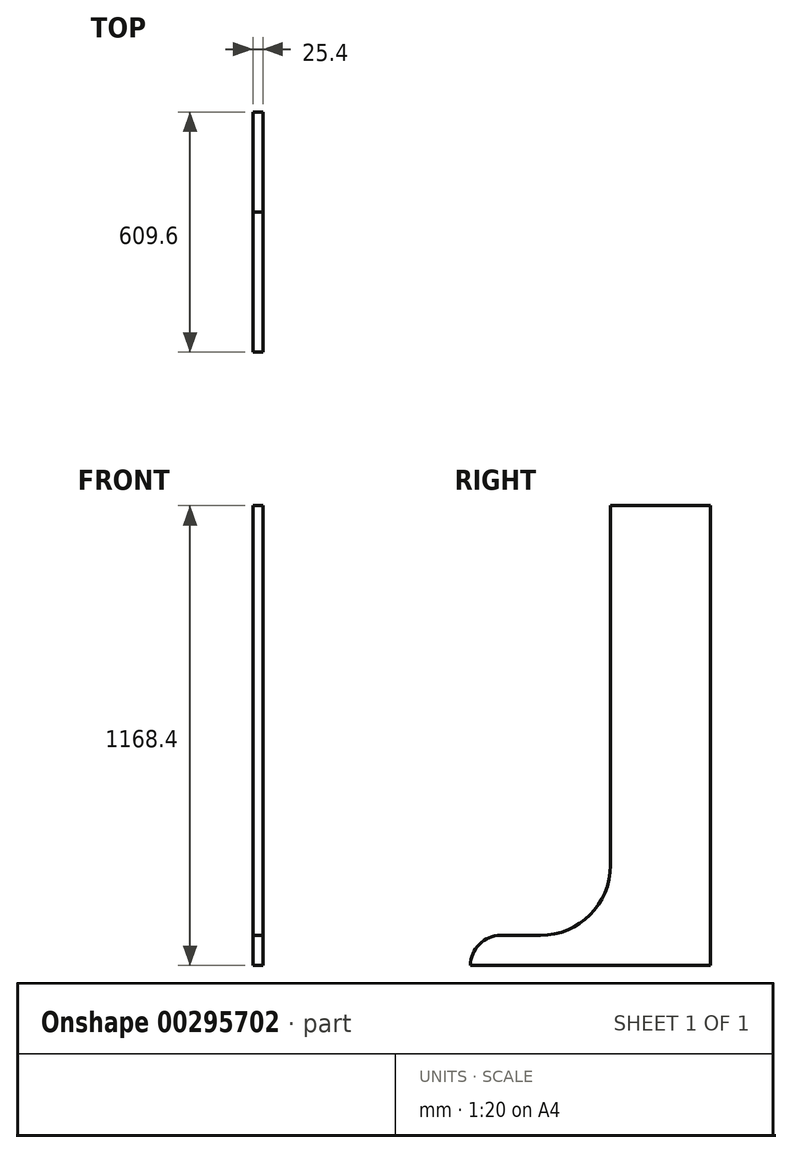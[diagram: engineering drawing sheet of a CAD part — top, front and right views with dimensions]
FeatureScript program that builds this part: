
annotation { "Feature Type Name" : "Feature", "Feature Type Description" : "" }
export const myFeature = defineFeature(function(context is Context, id is Id, definition is map)
    precondition{}
    {
        {
            var Q0;
            Q0=qCreatedBy(makeId("Right.planeOp"),FACE);
            var sketch = newSketch(context, id + "F0", { "sketchPlane" : qUnion([Q0])});
            skLineSegment(sketch, "E0.bottom", {"start": v(127, 584.2) * mm, "end": v(-127, 584.2) * mm});
            skLineSegment(sketch, "E0.top", {"start": v(127, -584.2) * mm, "end": v(-127, -584.2) * mm});
            skLineSegment(sketch, "E0.left", {"start": v(127, 584.2) * mm, "end": v(127, -584.2) * mm});
            skLineSegment(sketch, "E0.right", {"start": v(-127, 584.2) * mm, "end": v(-127, -584.2) * mm});
            skPoint(sketch, "E0.middle", {"position": v(0, 0) * mm});
            skLineSegment(sketch, "E1.bottom", {"start": v(-127, -584.2) * mm, "end": v(-482.6, -584.2) * mm});
            skLineSegment(sketch, "E1.top", {"start": v(-127, -330.2) * mm, "end": v(-482.6, -330.2) * mm});
            skLineSegment(sketch, "E1.left", {"start": v(-127, -584.2) * mm, "end": v(-127, -330.2) * mm});
            skLineSegment(sketch, "E1.right", {"start": v(-482.6, -584.2) * mm, "end": v(-482.6, -330.2) * mm});
            skSolve(sketch);
        }
        {
            var Q0;
            Q0 = qSketchRegion(id + "F0", true);
            extrude(context, id + "F1", {"entities" : qUnion([Q0]), "endBound" : BoundingType.SYMMETRIC, "depth" : 25.4 * mm});
        }
        {
            var Q0;
            Q0=makeQuery(id+"F1.opExtrude","CAP_FACE",FACE,{"disambiguationData":[OSD([sQuery(id+"F0.wireOp",EDGE,"E0.bottom"),sQuery(id+"F0.wireOp",EDGE,"E0.top"),sQuery(id+"F0.wireOp",EDGE,"E0.left"),sQuery(id+"F0.wireOp",EDGE,"E0.right"),sQuery(id+"F0.wireOp",EDGE,"E1.bottom"),sQuery(id+"F0.wireOp",EDGE,"E1.top"),sQuery(id+"F0.wireOp",EDGE,"E1.right")])],"isStart":false});
            var sketch = newSketch(context, id + "F2", { "sketchPlane" : qUnion([Q0])});
            skLineSegment(sketch, "E2", {"start": v(-482.6, -584.2) * mm, "end": v(-482.6, -584.2) * mm});
            skLineSegment(sketch, "E3", {"start": v(-127, -330.2) * mm, "end": v(-482.6, -330.2) * mm});
            skLineSegment(sketch, "E4", {"start": v(-482.6, -330.2) * mm, "end": v(-482.6, -584.2) * mm});
            skArc(sketch, "E5", {"start": v(-406.4, -508) * mm, "mid": v(-460.28, -530.32) * mm, "end": v(-482.6, -584.2) * mm});
            skLineSegment(sketch, "E6", {"start": v(-406.4, -508) * mm, "end": v(-304.8, -508) * mm});
            skArc(sketch, "E7.trimOffspring", {"start": v(-304.8, -508) * mm, "mid": v(-179.08, -455.92) * mm, "end": v(-127, -330.2) * mm});
            skPoint(sketch, "E8.center.orphan", {"position": v(-381, -330.2) * mm});
            skSolve(sketch);
        }
        {
            var Q0;
            Q0 = qSketchRegion(id + "F2", true);
            extrude(context, id + "F3", {"entities" : qUnion([Q0]), "operationType" : NewBodyOperationType.REMOVE, "endBound" : BoundingType.THROUGH_ALL, "oppositeDirection" : true, "depth" : 25.4 * mm});
        }
    });
